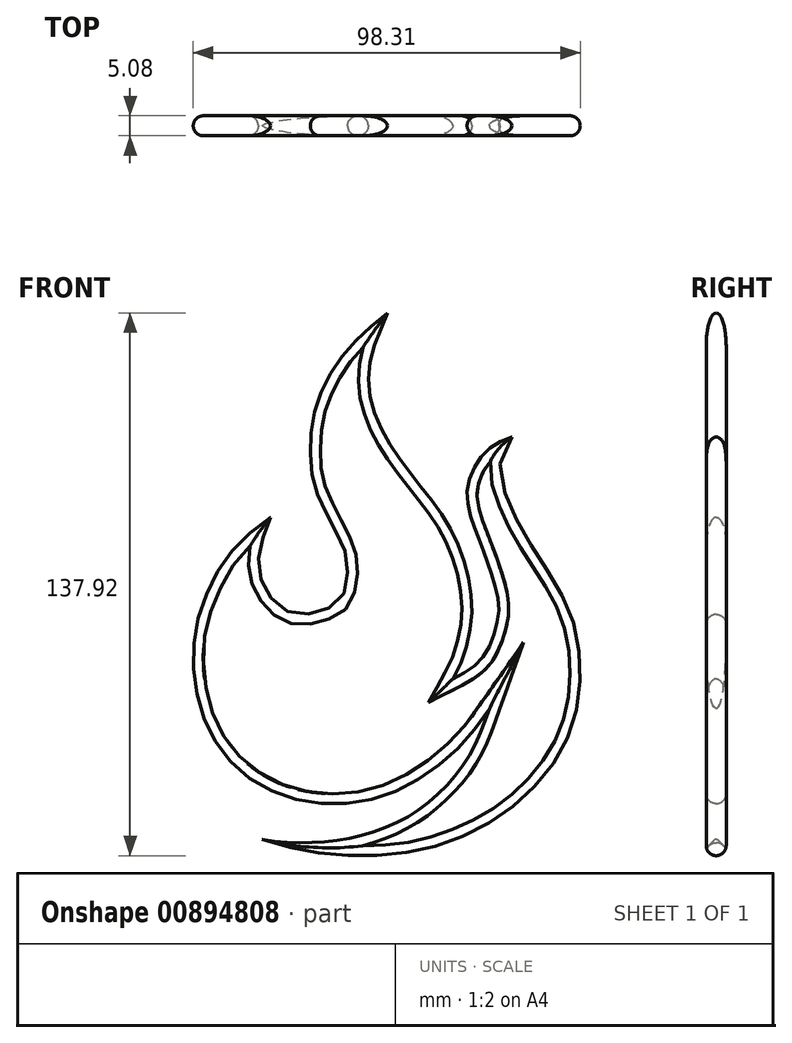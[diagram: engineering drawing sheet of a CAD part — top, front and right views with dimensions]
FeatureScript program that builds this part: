
annotation { "Feature Type Name" : "Feature", "Feature Type Description" : "" }
export const myFeature = defineFeature(function(context is Context, id is Id, definition is map)
    precondition{}
    {
        {
            var Q0;
            Q0=qCreatedBy(makeId("Front.planeOp"),FACE);
            var sketch = newSketch(context, id + "F0", { "sketchPlane" : qUnion([Q0])});
            skFitSpline(sketch, "E0", {"points": [v(0, 70.74) * mm, v(-10.48, 60.95) * mm, v(-18, 47.31) * mm, v(-19.57, 36.3) * mm, v(-18.7, 27.56) * mm, v(-15.72, 20.22) * mm, v(-12.58, 14.28) * mm, v(-10.3, 8.16) * mm, v(-10.48, 1.52) * mm, v(-12.75, -3.03) * mm, v(-20.62, -5.82) * mm, v(-26.38, -4.6) * mm, v(-31.63, 1.7) * mm, v(-32.68, 8.86) * mm, v(-31.1, 15.33) * mm, v(-29.7, 18.82) * mm], "startDerivative": vector(-122.33, -99.18) * mm, "endDerivative": vector(29.85, 69.6) * mm});
            skFitSpline(sketch, "E1", {"points": [v(-29.7, 18.82) * mm, v(-39.41, 10.35) * mm, v(-46.76, -2.78) * mm, v(-49.26, -14.97) * mm, v(-47.7, -28.89) * mm, v(-42.23, -40.3) * mm, v(-33.79, -48.27) * mm, v(-22.69, -52.96) * mm, v(-8.93, -53.74) * mm, v(2.17, -50.77) * mm, v(12.48, -44.52) * mm, v(20.14, -37.48) * mm, v(25.9, -29.87) * mm], "startDerivative": vector(-119.71, -88) * mm, "endDerivative": vector(74.36, 106.27) * mm});
            skFitSpline(sketch, "E2", {"points": [v(0, 70.74) * mm, v(-2.04, 65.61) * mm, v(-4.25, 59.3) * mm, v(-4.57, 50.62) * mm, v(-1.73, 41.62) * mm, v(2.54, 34.52) * mm, v(9.95, 24.73) * mm, v(14.65, 18.3) * mm, v(17.9, 12.07) * mm, v(19.83, 6.67) * mm, v(20.96, 1.52) * mm, v(21.48, -4.53) * mm, v(20.7, -11.65) * mm, v(18.62, -18.33) * mm, v(16.69, -22.2) * mm], "startDerivative": vector(-31.41, -80.16) * mm, "endDerivative": vector(-35.18, -64.05) * mm});
            skFitSpline(sketch, "E3", {"points": [v(25.9, -29.87) * mm, v(20.11, -42.87) * mm, v(9.23, -54.58) * mm, v(-1.55, -60.43) * mm, v(-14.29, -63.52) * mm, v(-27.84, -63.62) * mm, v(-31.85, -63) * mm], "startDerivative": vector(-25.64, -72.1) * mm, "endDerivative": vector(-34.16, 6.9) * mm});
            skFitSpline(sketch, "E4", {"points": [v(16.69, -22.2) * mm, v(24.09, -16.95) * mm, v(27.91, -7.69) * mm, v(28.04, -1.39) * mm, v(24.09, 11.1) * mm, v(20.84, 20.22) * mm, v(20.45, 26.66) * mm, v(22.99, 32.97) * mm, v(27.27, 37.25) * mm, v(31.66, 39.22) * mm], "startDerivative": vector(68.47, 34.85) * mm, "endDerivative": vector(51.33, 18.31) * mm});
            skFitSpline(sketch, "E5", {"points": [v(-31.85, -63) * mm, v(-18.94, -66.29) * mm, v(-2.2, -67.07) * mm, v(10.25, -65.28) * mm, v(22.26, -60.79) * mm, v(33.04, -53.72) * mm, v(42.47, -43.28) * mm, v(47.4, -32.47) * mm, v(48.98, -22.2) * mm, v(48.15, -11.61) * mm, v(45.14, -2.5) * mm, v(40.07, 6.13) * mm, v(33.45, 17) * mm, v(29.62, 25.9) * mm, v(28.8, 33.34) * mm, v(31.66, 39.22) * mm], "startDerivative": vector(169.1, -52.5) * mm, "endDerivative": vector(72.42, 110.49) * mm});
            skSolve(sketch);
        }
        {
            var Q0;
            Q0=makeQuery(id+"F0.imprint","IMPRINT",FACE,{"disambiguationData":[TD([[makeQuery(id+"F0.imprint","IMPRINT",EDGE,{"derivedFrom":sQuery(id+"F0.wireOp",EDGE,"E0")}),1.0]])]});
            extrude(context, id + "F1", {"entities" : qUnion([Q0]), "depth" : 2.54 * mm, "offsetDistance" : 25.4 * mm});
        }
        {
            var Q0;
            Q0=makeQuery(id+"F1.opExtrude","CAP_FACE",FACE,{"disambiguationData":[OSD([sQuery(id+"F0.wireOp",EDGE,"E0"),sQuery(id+"F0.wireOp",EDGE,"E1"),sQuery(id+"F0.wireOp",EDGE,"E2"),sQuery(id+"F0.wireOp",EDGE,"E3"),sQuery(id+"F0.wireOp",EDGE,"E4"),sQuery(id+"F0.wireOp",EDGE,"E5")])],"isStart":true});
            extrude(context, id + "F2", {"entities" : qUnion([Q0]), "operationType" : NewBodyOperationType.ADD, "depth" : 2.54 * mm, "offsetDistance" : 25.4 * mm});
        }
        {
            var Q0;
            Q0=makeQuery(id+"F1.opExtrude","CAP_EDGE",EDGE,{"disambiguationData":[OSD([sQuery(id+"F0.wireOp",EDGE,"E0")])],"isStart":false});
            var Q1;
            Q1=makeQuery(id+"F1.opExtrude","CAP_EDGE",EDGE,{"disambiguationData":[OSD([sQuery(id+"F0.wireOp",EDGE,"E3")])],"isStart":false});
            var Q2;
            Q2=makeQuery(id+"F1.opExtrude","CAP_EDGE",EDGE,{"disambiguationData":[OSD([sQuery(id+"F0.wireOp",EDGE,"E4")])],"isStart":false});
            var Q3;
            Q3=makeQuery(id+"F1.opExtrude","CAP_EDGE",EDGE,{"disambiguationData":[OSD([sQuery(id+"F0.wireOp",EDGE,"E2")])],"isStart":false});
            var Q4;
            Q4=makeQuery(id+"F1.opExtrude","CAP_EDGE",EDGE,{"disambiguationData":[OSD([sQuery(id+"F0.wireOp",EDGE,"E5")])],"isStart":false});
            var Q5;
            Q5=makeQuery(id+"F1.opExtrude","CAP_EDGE",EDGE,{"disambiguationData":[OSD([sQuery(id+"F0.wireOp",EDGE,"E1")])],"isStart":false});
            fillet(context, id + "F3", {"entities" : qUnion([Q0, Q1, Q2, Q3, Q4, Q5]), "radius" : 2.54 * mm, "tangentPropagation" : true, "allowEdgeOverflow" : false});
        }
        {
            var Q0;
            Q0=makeQuery(id+"F2.opExtrude","CAP_FACE",FACE,{"disambiguationData":[OSD([sQuery(id+"F0.wireOp",EDGE,"E0"),sQuery(id+"F0.wireOp",EDGE,"E1"),sQuery(id+"F0.wireOp",EDGE,"E2"),sQuery(id+"F0.wireOp",EDGE,"E3"),sQuery(id+"F0.wireOp",EDGE,"E4"),sQuery(id+"F0.wireOp",EDGE,"E5")])],"isStart":false});
            fillet(context, id + "F4", {"entities" : qUnion([Q0]), "radius" : 2.54 * mm, "tangentPropagation" : true, "allowEdgeOverflow" : false});
        }
    });
